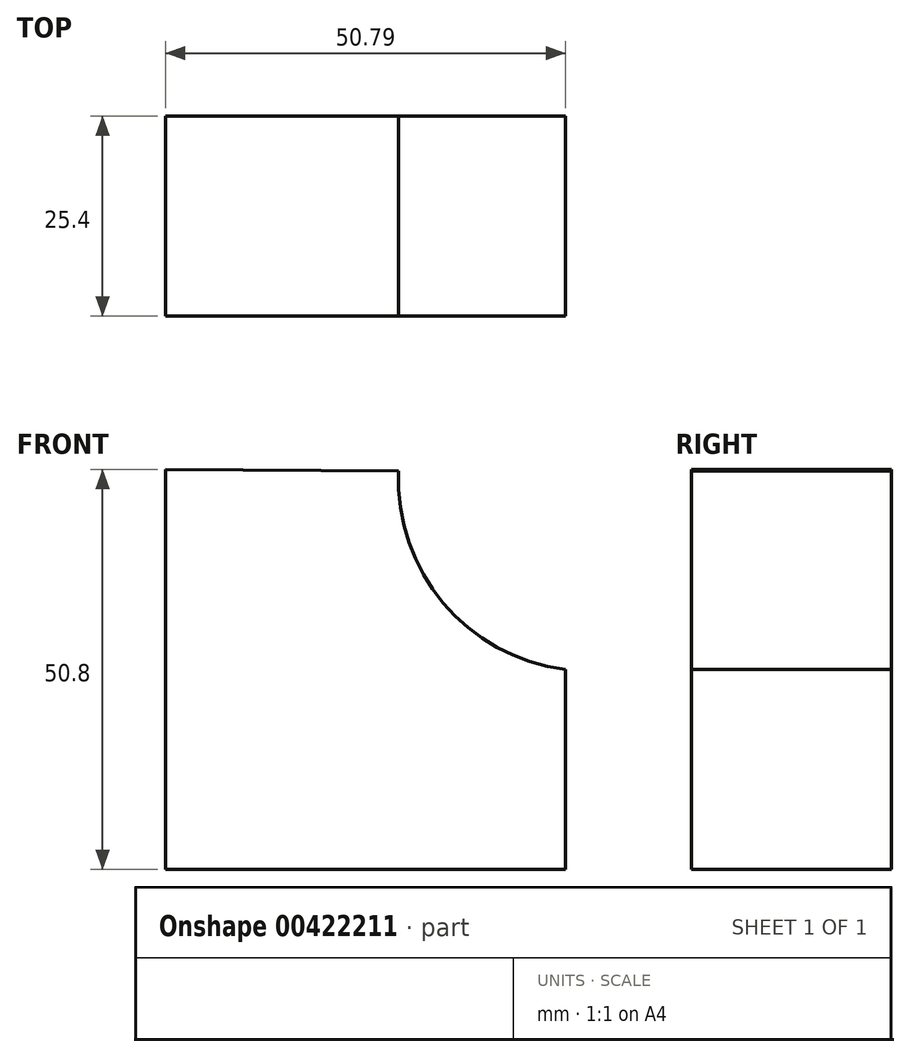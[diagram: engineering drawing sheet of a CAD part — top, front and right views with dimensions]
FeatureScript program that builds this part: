
annotation { "Feature Type Name" : "Feature", "Feature Type Description" : "" }
export const myFeature = defineFeature(function(context is Context, id is Id, definition is map)
    precondition{}
    {
        {
            var Q0;
            Q0=qCreatedBy(makeId("Front.planeOp"),FACE);
            var sketch = newSketch(context, id + "F0", { "sketchPlane" : qUnion([Q0])});
            skLineSegment(sketch, "E0", {"start": v(-66.07, 67.6) * mm, "end": v(-66.07, 16.8) * mm});
            skLineSegment(sketch, "E1", {"start": v(-66.07, 16.8) * mm, "end": v(-15.28, 16.8) * mm});
            skLineSegment(sketch, "E2", {"start": v(-15.28, 16.8) * mm, "end": v(-15.28, 42.2) * mm});
            skArc(sketch, "E3", {"start": v(-36.47, 67.4) * mm, "mid": v(-30.8, 50.65) * mm, "end": v(-15.28, 42.2) * mm});
            skLineSegment(sketch, "E4", {"start": v(-66.07, 67.6) * mm, "end": v(-36.47, 67.4) * mm});
            skSolve(sketch);
        }
        {
            var Q0;
            Q0 = qSketchRegion(id + "F0", true);
            var Q1;
            Q1=makeQuery(id+"F0.imprint","IMPRINT",FACE,{"disambiguationData":[TD([[makeQuery(id+"F0.imprint","IMPRINT",EDGE,{"derivedFrom":sQuery(id+"F0.wireOp",EDGE,"E0")}),1.0]])]});
            extrude(context, id + "F1", {"entities" : qUnion([Q0, Q1]), "depth" : 25.4 * mm});
        }
    });
